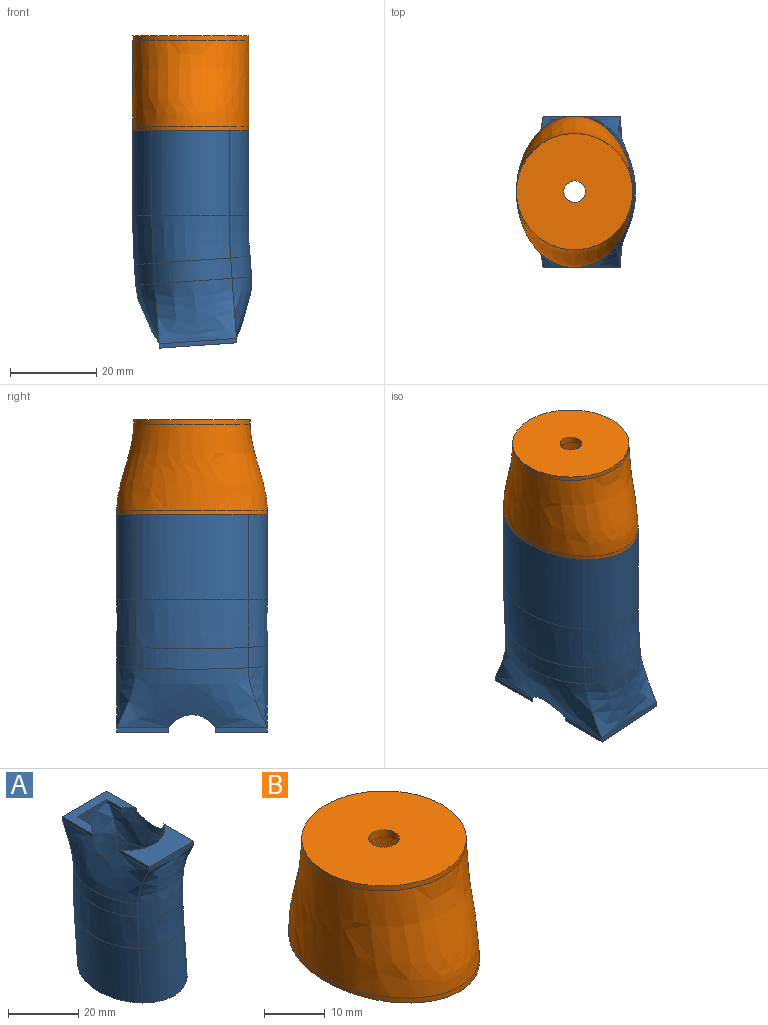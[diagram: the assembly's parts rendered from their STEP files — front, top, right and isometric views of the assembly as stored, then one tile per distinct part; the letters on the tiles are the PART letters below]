
ASSEMBLY  parts=2 mates=1
PART A: 51 faces, bbox 31x38.1x53.1 mm
  f0: plane 12.09x1mm, normal (-1,0,0), area 12.1mm2, adj f2,f9,f14,f25
  f1: plane 12.09x1mm, normal (1,0,0), area 12.1mm2, adj f2,f9,f12,f25
  f2: plane 18x12.09mm, normal (0,0,1), area 97.1mm2, adj f0,f1,f9,f22,f23,f24,f25
  f3: plane 16.59x10.26mm, normal (0,0,-1), area 110.2mm2, adj f15,f17,f18,f20,f21,f25
  f4: plane 6.74x0.11mm, normal (1,0,0), area 0.4mm2, adj f15,f16,f25
  f5: plane 7.94x1.16mm, normal (-1,0,0), area 0.4mm2, adj f16,f20,f25
  f6: plane 12.09x1mm, normal (-1,0,0), area 12.1mm2, adj f7,f10,f14,f25
  f7: plane 18x1mm, normal (0,-1,0), area 18mm2, adj f6,f8,f10,f13
  f8: plane 12.09x1mm, normal (1,0,0), area 12.1mm2, adj f7,f10,f12,f25
  f9: plane 18x1mm, normal (0,1,0), area 18mm2, adj f0,f1,f2,f11
  f10: plane 18x12.09mm, normal (0,0,1), area 152.8mm2, adj f6,f7,f8,f25
  f11: bspline ~18.36x14.14mm, area 273mm2, adj f9,f12,f14,f41
  f12: bspline ~35.22x14.23mm, area 439mm2, adj f1,f8,f11,f13,f25,f42
  f13: bspline ~18.06x14.14mm, area 274.3mm2, adj f7,f12,f14,f39
  f14: bspline ~35.23x14.23mm, area 438.1mm2, adj f0,f6,f11,f13,f25,f40
  f15: offset ~38.13x16.43mm, area 347.1mm2, adj f3,f4,f16,f17,f19,f21,f25,f28
  f16: plane 16.58x10.25mm, normal (0,0,-1), area 54.4mm2, adj f4,f5,f15,f19,f20,f22,f23,f24
  f17: plane 6.76x0.12mm, normal (1,0,0), area 0.4mm2, adj f3,f15,f25
  f18: plane 8.12x1.16mm, normal (-1,0,0), area 0.4mm2, adj f3,f20,f25
  f19: offset ~20.56x16.25mm, area 234.6mm2, adj f15,f16,f20,f27
  f20: offset ~38.13x16.43mm, area 345.1mm2, adj f3,f5,f16,f18,f19,f21,f25,f26
  f21: offset ~20.26x16.25mm, area 235.7mm2, adj f3,f15,f20,f29
  f22: plane 5.93x1.1mm, normal (-1,0,0), area 6.5mm2, adj f2,f16,f23,f25
  f23: plane 12x1.1mm, normal (0,-1,0), area 13.2mm2, adj f2,f16,f22,f24
  f24: plane 5.93x1.1mm, normal (1,0,0), area 6.5mm2, adj f2,f16,f23,f25
  f25: cylinder r=10.5mm len=21mm, axis (0,0,1), area 107.4mm2, adj f0,f1,f2,f3,f4,f5,f6,f8
  f26: bspline ~24.68x4.76mm, area 126.9mm2, adj f20,f27,f29,f30
  f27: bspline ~16.3x4.76mm, area 89.4mm2, adj f19,f26,f28,f31
  f28: bspline ~24.6x4.76mm, area 126.4mm2, adj f15,f27,f29,f32
  f29: bspline ~16.39x4.76mm, area 90.1mm2, adj f21,f26,f28,f33
  f30: bspline ~24.68x9.9mm, area 258.6mm2, adj f26,f31,f33,f34
  f31: bspline ~16.64x11.03mm, area 196.7mm2, adj f27,f30,f32,f35
  f32: bspline ~24.6x11.33mm, area 298.4mm2, adj f28,f31,f33,f36
  f33: bspline ~16.73x11.04mm, area 198.1mm2, adj f29,f30,f32,f37
  f34: bspline ~24.68x20.01mm, area 526.6mm2, adj f30,f35,f37,f38
  f35: bspline ~20.85x17.63mm, area 371.1mm2, adj f31,f34,f36,f38
  f36: bspline ~24.6x20.01mm, area 524.5mm2, adj f32,f35,f37,f38
  f37: bspline ~20.86x17.72mm, area 373.8mm2, adj f33,f34,f36,f38
  f38: plane 35.48x27.42mm, normal (0.07,0,-1), area 103.5mm2, adj f34,f35,f36,f37,f47,f48,f49,f50
  f39: bspline ~18.06x4.76mm, area 99.1mm2, adj f13,f40,f42,f43
  f40: bspline ~26.04x4.76mm, area 133.8mm2, adj f14,f39,f41,f44
  f41: bspline ~17.96x4.76mm, area 98.4mm2, adj f11,f40,f42,f45
  f42: bspline ~26.12x4.76mm, area 134.4mm2, adj f12,f39,f41,f46
  f43: bspline ~18.4x11.1mm, area 218mm2, adj f39,f44,f46,f47
  f44: bspline ~26.04x11.41mm, area 317.9mm2, adj f40,f43,f45,f48
  f45: bspline ~18.3x11.09mm, area 216.4mm2, adj f41,f44,f46,f49
  f46: bspline ~26.12x9.84mm, area 271.8mm2, adj f42,f43,f45,f50
  f47: bspline ~20.97x19.39mm, area 411.3mm2, adj f38,f43,f48,f50
  f48: bspline ~26.04x20.03mm, area 555.4mm2, adj f38,f44,f47,f49
  f49: bspline ~20.97x19.29mm, area 408.3mm2, adj f38,f45,f48,f50
  f50: bspline ~26.12x20.03mm, area 557.6mm2, adj f38,f46,f47,f49
PART B: 9 faces, bbox 32.8x35x22 mm
  f0: cylinder r=13.5mm len=27mm, axis (0,0,-1), area 84.8mm2, adj f1,f4
  f1: plane 27x27mm, normal (0,0,1), area 552.9mm2, adj f0,f7
  f2: extruded ~35x27mm, area 97.8mm2, adj f3,f4
  f3: plane 35x27mm, normal (0,0,-1), area 320.6mm2, adj f2,f8
  f4: bspline ~35x27mm, area 1839.9mm2, adj f0,f2
  f5: cylinder r=6.58mm len=15.5mm, axis (0,0,1), area 641.2mm2, adj f6,f8
  f6: plane 13.17x13.17mm, normal (0,0,-1), area 116.6mm2, adj f5,f7
  f7: cylinder r=2.5mm len=5mm, axis (0,0,1), area 23.6mm2, adj f1,f6
  f8: torus R=11.58mm, axis (0,0,1), area 414.6mm2, adj f3,f5
PLACE A rot(axis=(1,0,0.03),180deg) t=(-15.49,-14.51,-53.71)mm
PLACE B t=(-61.36,-14.51,-43.74)mm
MATE fastened A.f38 <-> B.f0  axis (0,0,1) through (-16.19,-14.51,-18.74)mm
